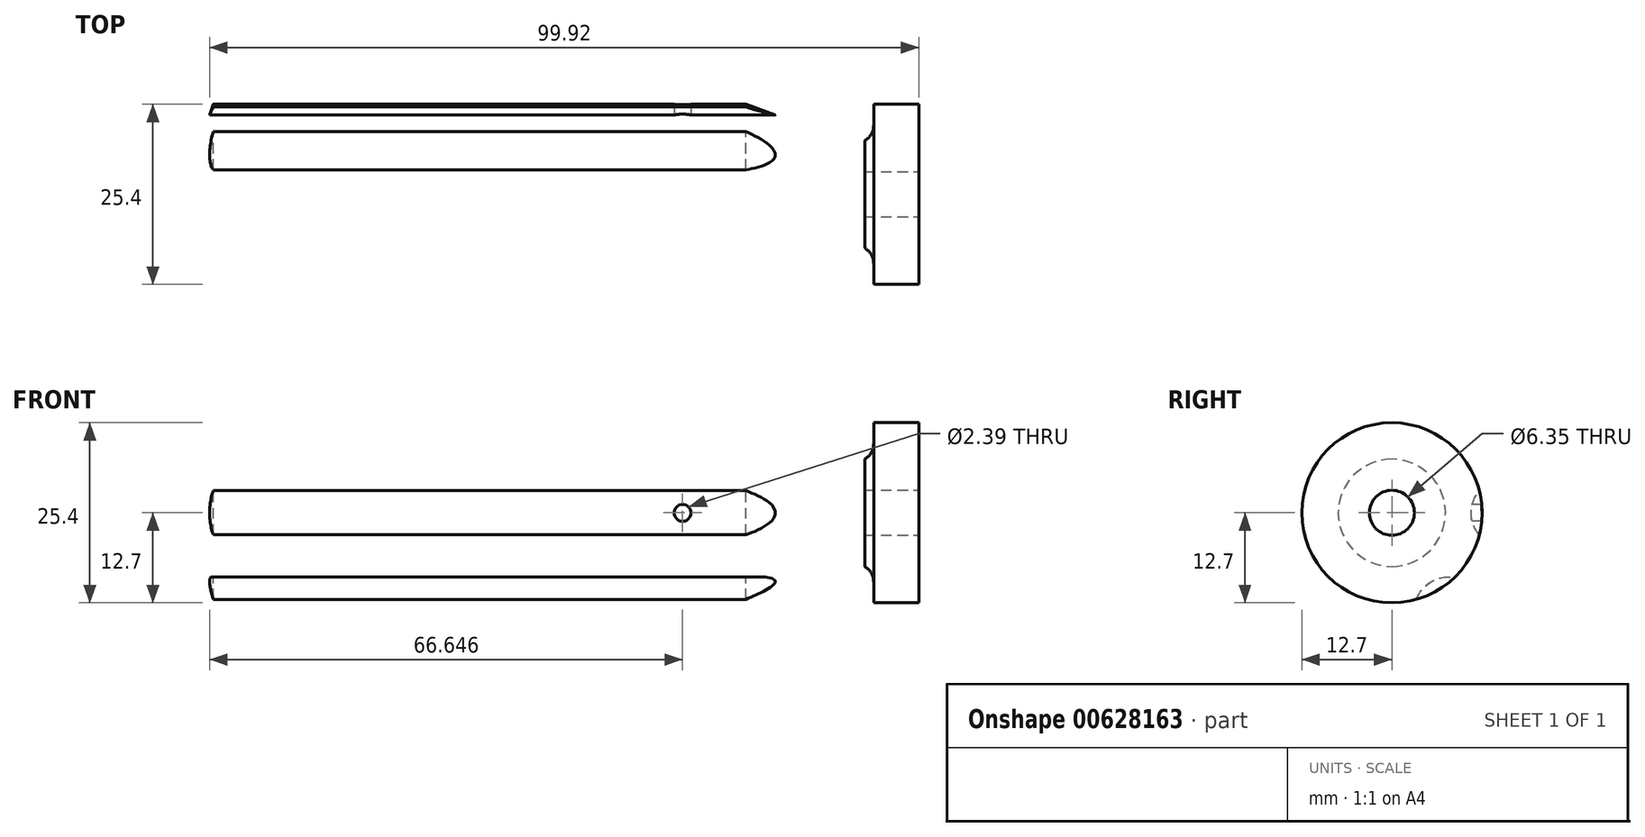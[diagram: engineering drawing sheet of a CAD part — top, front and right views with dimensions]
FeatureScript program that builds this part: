
annotation { "Feature Type Name" : "Feature", "Feature Type Description" : "" }
export const myFeature = defineFeature(function(context is Context, id is Id, definition is map)
    precondition{}
    {
        {
            var Q0;
            Q0=qCreatedBy(makeId("Front.planeOp"),FACE);
            var sketch = newSketch(context, id + "F0", { "sketchPlane" : qUnion([Q0])});
            skLineSegment(sketch, "E0", {"start": v(0, 3.18) * mm, "end": v(-40.64, 3.18) * mm});
            skLineSegment(sketch, "E1", {"start": v(-40.64, 3.17) * mm, "end": v(-40.64, 0) * mm});
            skLineSegment(sketch, "E2", {"start": v(-40.64, 0) * mm, "end": v(-101.6, 0) * mm});
            skLineSegment(sketch, "E3", {"start": v(-99.42, 12.7) * mm, "end": v(-24.38, 12.7) * mm});
            skLineSegment(sketch, "E4", {"start": v(-24.38, 12.7) * mm, "end": v(-9.76, 7.38) * mm});
            skLineSegment(sketch, "E5", {"start": v(-6.35, 9.76) * mm, "end": v(-6.35, 12.7) * mm});
            skLineSegment(sketch, "E6", {"start": v(-6.35, 12.7) * mm, "end": v(0, 12.7) * mm});
            skLineSegment(sketch, "E7", {"start": v(0, 12.7) * mm, "end": v(0, 3.18) * mm});
            skPoint(sketch, "E8.visualSharp", {"position": v(-6.35, 6.14) * mm});
            skArc(sketch, "E8.filletArc", {"start": v(-9.76, 7.38) * mm, "mid": v(-7.43, 7.68) * mm, "end": v(-6.35, 9.76) * mm});
            skArc(sketch, "E9", {"start": v(-99.42, 12.7) * mm, "mid": v(-101.05, 6.44) * mm, "end": v(-101.6, 0) * mm});
            skPoint(sketch, "E10.orphan", {"position": v(-101.6, 12.7) * mm});
            skSolve(sketch);
        }
        {
            var Q0;
            Q0=makeQuery(id+"F0.imprint","IMPRINT",FACE,{"disambiguationData":[TD([[makeQuery(id+"F0.imprint","IMPRINT",EDGE,{"derivedFrom":sQuery(id+"F0.wireOp",EDGE,"E0")}),-1.0]])]});
            var Q1;
            Q1=sQuery(id+"F0.wireOp",EDGE,"E2");
            revolve(context, id + "F1", {"entities" : qUnion([Q0]), "axis" : qUnion([Q1]), "revolveType" : RevolveType.FULL});
        }
        {
            var Q0;
            Q0=qCreatedBy(makeId("Right.planeOp"),FACE);
            var sketch = newSketch(context, id + "F2", { "sketchPlane" : qUnion([Q0])});
            skCircle(sketch, "E11", {"center": v(0, 0) * mm, "radius": 16 * mm});
            skCircle(sketch, "E12", {"center": v(-16, 0) * mm, "radius": 4.83 * mm});
            skCircle(sketch, "E13.1.0", {"center": v(-8, -13.86) * mm, "radius": 4.83 * mm});
            skCircle(sketch, "E13.2.0", {"center": v(8, -13.86) * mm, "radius": 4.83 * mm});
            skCircle(sketch, "E13.3.0", {"center": v(16, 0) * mm, "radius": 4.83 * mm});
            skCircle(sketch, "E13.4.0", {"center": v(8, 13.86) * mm, "radius": 4.83 * mm});
            skCircle(sketch, "E13.5.0", {"center": v(-8, 13.86) * mm, "radius": 4.83 * mm});
            skSolve(sketch);
        }
        {
            var Q0;
            Q0=qCreatedBy(makeId("Right.planeOp"),FACE);
            var sketch = newSketch(context, id + "F3", { "sketchPlane" : qUnion([Q0])});
            skCircle(sketch, "E14", {"center": v(0, 0) * mm, "radius": 16 * mm});
            skCircle(sketch, "E15", {"center": v(-16, 0) * mm, "radius": 4.83 * mm});
            skCircle(sketch, "E16.1.0", {"center": v(-8, -13.86) * mm, "radius": 4.83 * mm});
            skCircle(sketch, "E16.2.0", {"center": v(8, -13.86) * mm, "radius": 4.83 * mm});
            skCircle(sketch, "E16.3.0", {"center": v(16, 0) * mm, "radius": 4.83 * mm});
            skCircle(sketch, "E16.4.0", {"center": v(8, 13.86) * mm, "radius": 4.83 * mm});
            skCircle(sketch, "E16.5.0", {"center": v(-8, 13.86) * mm, "radius": 4.83 * mm});
            skSolve(sketch);
        }
        {
            var Q0;
            {var subQ0=sQuery(id+"F2.wireOp",EDGE,"E13.5.0");var subQ1=sQuery(id+"F2.wireOp",EDGE,"E11");var subQ2=makeQuery(id+"F2.imprint","INTERSECT",VERTEX,{"disambiguationData":[OD(0.0)],"derivedFrom":[subQ1,subQ0]});Q0=makeQuery(id+"F2.imprint","IMPRINT",FACE,{"disambiguationData":[TD([[makeQuery(id+"F2.imprint","IMPRINT",EDGE,{"disambiguationData":[TD([[subQ2,-1.0]])],"derivedFrom":subQ1}),1.0]])]});}
            var Q1;
            {var subQ0=sQuery(id+"F2.wireOp",EDGE,"E13.4.0");var subQ1=sQuery(id+"F2.wireOp",EDGE,"E11");var subQ2=makeQuery(id+"F2.imprint","INTERSECT",VERTEX,{"disambiguationData":[OD(0.0)],"derivedFrom":[subQ1,subQ0]});Q1=makeQuery(id+"F2.imprint","IMPRINT",FACE,{"disambiguationData":[TD([[makeQuery(id+"F2.imprint","IMPRINT",EDGE,{"disambiguationData":[TD([[subQ2,-1.0]])],"derivedFrom":subQ1}),1.0]])]});}
            var Q2;
            {var subQ0=sQuery(id+"F2.wireOp",EDGE,"E13.3.0");var subQ1=sQuery(id+"F2.wireOp",EDGE,"E11");var subQ2=makeQuery(id+"F2.imprint","INTERSECT",VERTEX,{"disambiguationData":[OD(0.0)],"derivedFrom":[subQ1,subQ0]});Q2=makeQuery(id+"F2.imprint","IMPRINT",FACE,{"disambiguationData":[TD([[makeQuery(id+"F2.imprint","IMPRINT",EDGE,{"disambiguationData":[TD([[subQ2,1.0]])],"derivedFrom":subQ1}),1.0]])]});}
            var Q3;
            {var subQ0=sQuery(id+"F2.wireOp",EDGE,"E13.2.0");var subQ1=sQuery(id+"F2.wireOp",EDGE,"E11");var subQ2=makeQuery(id+"F2.imprint","INTERSECT",VERTEX,{"disambiguationData":[OD(0.0)],"derivedFrom":[subQ1,subQ0]});Q3=makeQuery(id+"F2.imprint","IMPRINT",FACE,{"disambiguationData":[TD([[makeQuery(id+"F2.imprint","IMPRINT",EDGE,{"disambiguationData":[TD([[subQ2,-1.0]])],"derivedFrom":subQ1}),1.0]])]});}
            var Q4;
            {var subQ0=sQuery(id+"F2.wireOp",EDGE,"E13.1.0");var subQ1=sQuery(id+"F2.wireOp",EDGE,"E11");var subQ2=makeQuery(id+"F2.imprint","INTERSECT",VERTEX,{"disambiguationData":[OD(0.0)],"derivedFrom":[subQ1,subQ0]});Q4=makeQuery(id+"F2.imprint","IMPRINT",FACE,{"disambiguationData":[TD([[makeQuery(id+"F2.imprint","IMPRINT",EDGE,{"disambiguationData":[TD([[subQ2,-1.0]])],"derivedFrom":subQ1}),1.0]])]});}
            var Q5;
            {var subQ0=sQuery(id+"F2.wireOp",EDGE,"E12");var subQ1=sQuery(id+"F2.wireOp",EDGE,"E11");var subQ2=makeQuery(id+"F2.imprint","INTERSECT",VERTEX,{"disambiguationData":[OD(0.0)],"derivedFrom":[subQ1,subQ0]});Q5=makeQuery(id+"F2.imprint","IMPRINT",FACE,{"disambiguationData":[TD([[makeQuery(id+"F2.imprint","IMPRINT",EDGE,{"disambiguationData":[TD([[subQ2,-1.0]])],"derivedFrom":subQ1}),1.0]])]});}
            extrude(context, id + "F4", {"entities" : qUnion([Q0, Q1, Q2, Q3, Q4, Q5]), "operationType" : NewBodyOperationType.REMOVE, "endBound" : BoundingType.THROUGH_ALL, "oppositeDirection" : true, "depth" : 25.4 * mm, "offsetDistance" : 25.4 * mm, "hasSecondDirection" : true, "secondDirectionOppositeDirection" : true, "secondDirectionDepth" : 7.62 * mm});
        }
        {
            var Q0;
            Q0=qCreatedBy(makeId("Front.planeOp"),FACE);
            var sketch = newSketch(context, id + "F5", { "sketchPlane" : qUnion([Q0])});
            skCircle(sketch, "E17", {"center": v(-33.27, 0) * mm, "radius": 1.2 * mm});
            skSolve(sketch);
        }
        {
            var Q0;
            Q0 = qSketchRegion(id + "F5", true);
            extrude(context, id + "F6", {"entities" : qUnion([Q0]), "operationType" : NewBodyOperationType.REMOVE, "endBound" : BoundingType.SYMMETRIC, "oppositeDirection" : true, "depth" : 25.4 * mm, "offsetDistance" : 25.4 * mm});
        }
    });
